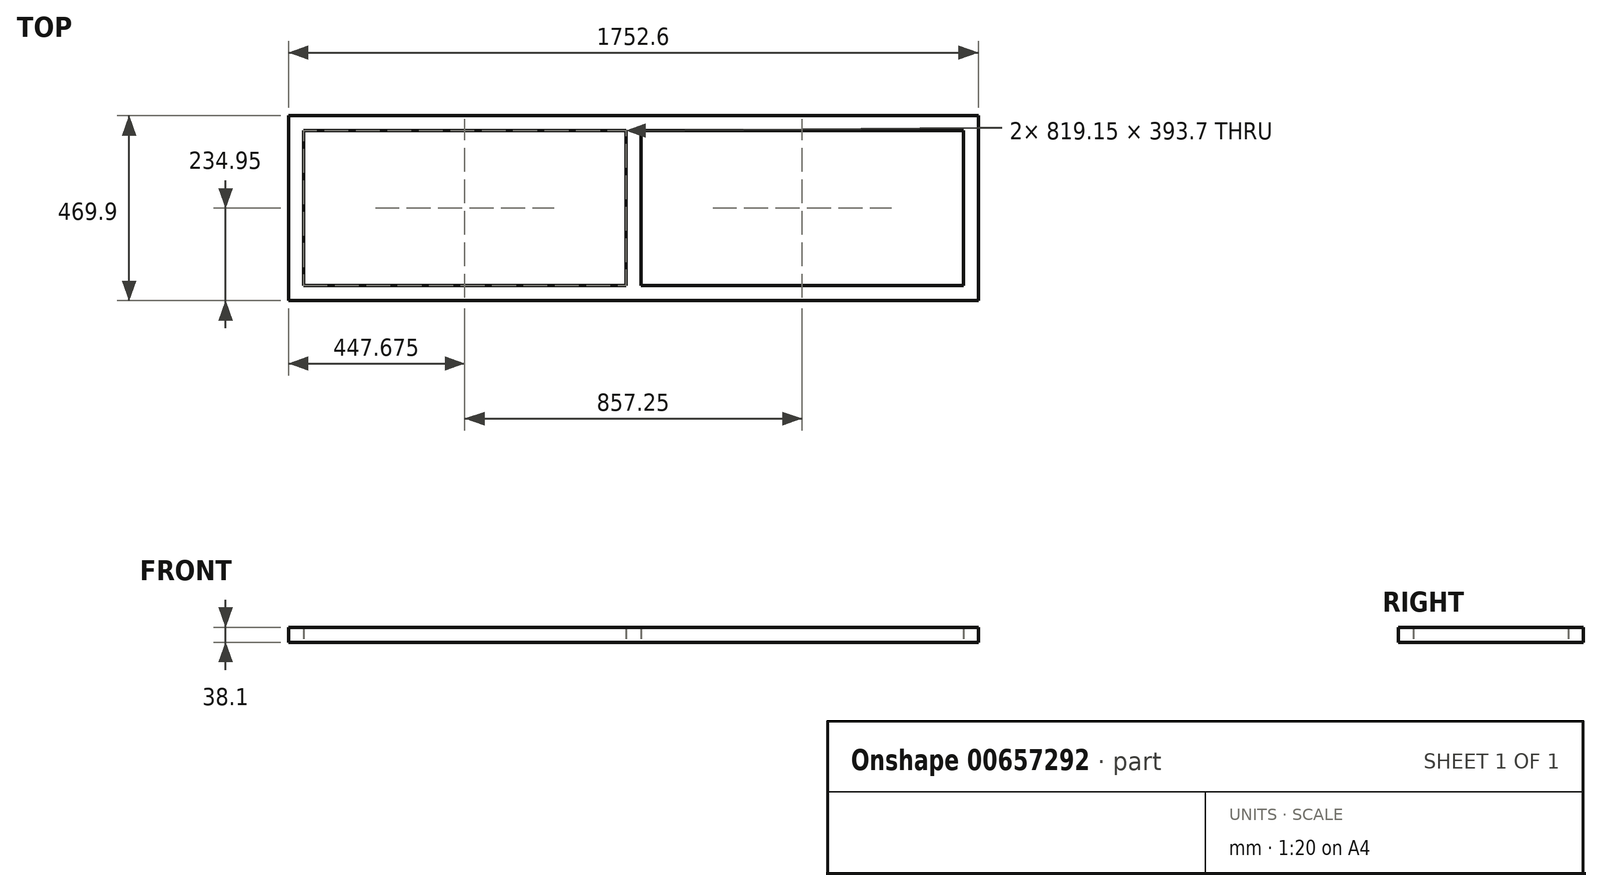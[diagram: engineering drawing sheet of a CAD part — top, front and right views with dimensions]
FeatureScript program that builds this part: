
annotation { "Feature Type Name" : "Feature", "Feature Type Description" : "" }
export const myFeature = defineFeature(function(context is Context, id is Id, definition is map)
    precondition{}
    {
        {
            var Q0;
            Q0=qCreatedBy(makeId("Top.planeOp"),FACE);
            var sketch = newSketch(context, id + "F0", { "sketchPlane" : qUnion([Q0])});
            skLineSegment(sketch, "E0.bottom", {"start": v(0, 0) * mm, "end": v(1752.6, 0) * mm});
            skLineSegment(sketch, "E0.top", {"start": v(0, 469.9) * mm, "end": v(1752.6, 469.9) * mm});
            skLineSegment(sketch, "E0.left", {"start": v(0, 0) * mm, "end": v(0, 469.9) * mm});
            skLineSegment(sketch, "E0.right", {"start": v(1752.6, 0) * mm, "end": v(1752.6, 469.9) * mm});
            skLineSegment(sketch, "E1.0", {"start": v(38.1, 431.8) * mm, "end": v(857.25, 431.8) * mm});
            skLineSegment(sketch, "E1.1", {"start": v(38.1, 38.1) * mm, "end": v(38.1, 431.8) * mm});
            skLineSegment(sketch, "E1.2", {"start": v(38.1, 38.1) * mm, "end": v(857.25, 38.1) * mm});
            skLineSegment(sketch, "E1.3", {"start": v(1714.5, 38.1) * mm, "end": v(1714.5, 431.8) * mm});
            skLineSegment(sketch, "E2.0", {"start": v(895.35, 38.1) * mm, "end": v(895.35, 431.8) * mm});
            skLineSegment(sketch, "E3.0", {"start": v(857.25, 38.1) * mm, "end": v(857.25, 431.8) * mm});
            skLineSegment(sketch, "E4.trimOffspring", {"start": v(895.35, 38.1) * mm, "end": v(1714.5, 38.1) * mm});
            skLineSegment(sketch, "E5.trimOffspring", {"start": v(895.35, 431.8) * mm, "end": v(1714.5, 431.8) * mm});
            skSolve(sketch);
        }
        {
            var Q0;
            Q0=makeQuery(id+"F0.imprint","IMPRINT",FACE,{"disambiguationData":[TD([[makeQuery(id+"F0.imprint","IMPRINT",EDGE,{"derivedFrom":sQuery(id+"F0.wireOp",EDGE,"E0.bottom")}),1.0]])]});
            extrude(context, id + "F1", {"entities" : qUnion([Q0]), "depth" : 38.1 * mm, "offsetDistance" : 25.4 * mm});
        }
    });
